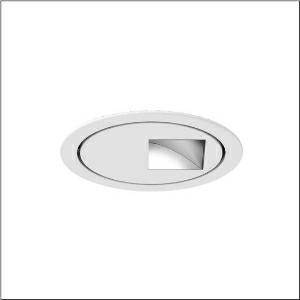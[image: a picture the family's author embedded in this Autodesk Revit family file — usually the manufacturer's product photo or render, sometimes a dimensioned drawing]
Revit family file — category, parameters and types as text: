
# Revit family: lunis_11_mini_round_51dk11cd2wn21
name_source: partatom
category: Lighting Fixtures
units: mm (PartAtom-declared; Revit-internal decimal feet)

## family parameters
Cut with Voids When Loaded = No
Host = Face
Light Source = No
Part Type = Normal
Room Calculation Point = No
Round Connector Dimension = Use Diameter
Shared = No

## types (1)
- Lunis 11 mini round (1 x LED 4000K / CRI = 90 (unbekannt), 2120 lm, 4000K)
    Apparent Load = 28 VA
    CIE Flux Codes = 44 77 97 100 100
    Color Rendering = 90
    Color Temperature = 4000K
    Default Elevation = 1800 mm
    Description = Lunis 11 mini round, downlight, light control with wallwasher, of highly reflective aluminium, highly specular, light emission: direct distribution, LED rated luminous flux: 2.120lm, light colour: 940, control gear: ECG, with terminal, 5-pole, mains connection: 220..230V, AC/DC, 0/50..60Hz, LED module, luminaire module, of aluminium, highly specular, white, diameter: 176mm, clamping range: 1..40mm, recessing ring, of plastic, traffic white (RAL 9016), protection rating (complete): IP20, insulation class (complete): insulation class II (safety insulation), certification: CE, permissible ambient temperature for indoor applications: 0..+35°C, packaging unit: 1 piece
    Height = 0 mm  [stored 0 ft]
    Lamp = 1 x LED 4000K / CRI >= 90 (unbekannt)
    Lamp Light Flux = 2120 lm
    Lamp count = 1
    Length = 176 mm
    Luminous efficacy = 76 lm/W
    Manufacturer = Siteco
    ModVariant = No
    Model = 51DK11CD2WN21
    Mounting Place = Ceiling
    Mounting Type = Recessed
    Number of Poles = 1
    OnlyDefault = Yes
    Power Factor = 1
    Product Name = Lunis 11 mini round
    Product group = downlight | ceiling recessed
    ProductGroupID = 402
    Protection Class = Protection class II
    Protection Degree = IP 20
    RLX_Detail_Level = 1
    RlxData = <blob elided: 59413 chars, md5=f8df8d52>
    Socket = socket
    Standby Power = 0 W
    System Light Flux = 2120 lm
    System Power = 28 W
    Type Comments = Product without accessories
    Type Image = l_1004772.jpg
    URL = http://relux.com
    VarID = ---
    Voltage = 0 V
    Weight = 0.00 kg
    Width = 176 mm

note: [stored X ft] marks values corroborated as IEEE doubles in the binary element streams (Revit-internal decimal feet)

## geometry (parser evidence)
native form markers: Blend x4, Sweep x10
no freeform markers — native parametric forms only
